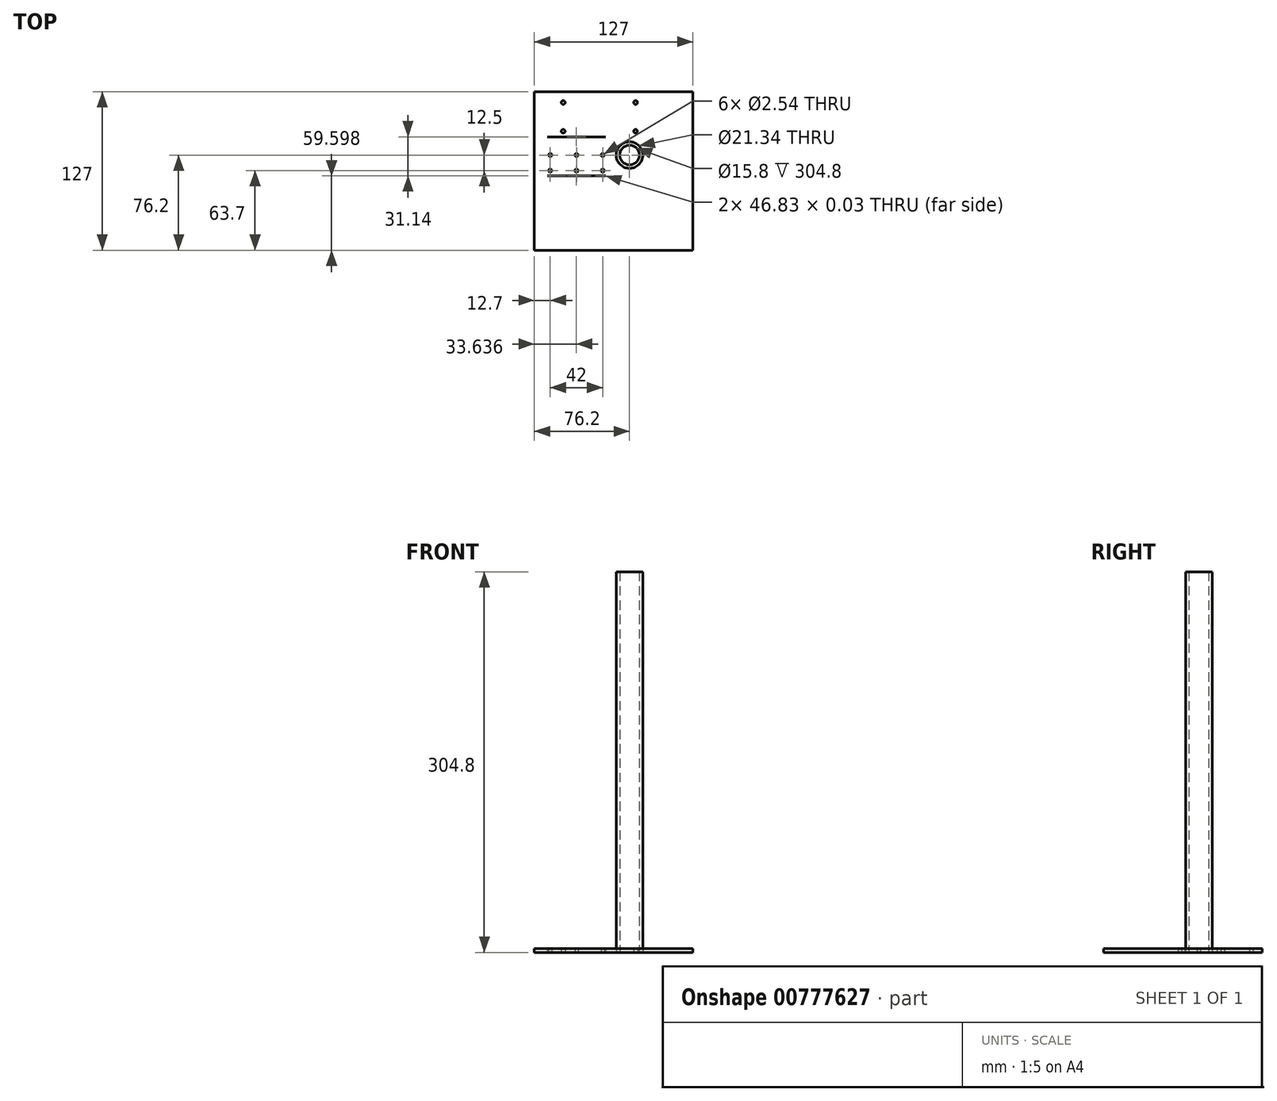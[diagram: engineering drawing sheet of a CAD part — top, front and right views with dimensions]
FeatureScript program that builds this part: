
annotation { "Feature Type Name" : "Feature", "Feature Type Description" : "" }
export const myFeature = defineFeature(function(context is Context, id is Id, definition is map)
    precondition{}
    {
        {
            var Q0;
            Q0=qCreatedBy(makeId("Top.planeOp"),FACE);
            var sketch = newSketch(context, id + "F0", { "sketchPlane" : qUnion([Q0])});
            skCircle(sketch, "E0", {"center": v(0, 0) * mm, "radius": 10.67 * mm});
            skCircle(sketch, "E1", {"center": v(0, 0) * mm, "radius": 7.9 * mm});
            skSolve(sketch);
        }
        {
            var Q0;
            Q0=makeQuery(id+"F0.imprint","IMPRINT",FACE,{"disambiguationData":[TD([[makeQuery(id+"F0.imprint","IMPRINT",EDGE,{"derivedFrom":sQuery(id+"F0.wireOp",EDGE,"E0")}),1.0]])]});
            extrude(context, id + "F1", {"entities" : qUnion([Q0]), "depth" : 304.8 * mm, "offsetDistance" : 25.4 * mm});
        }
        {
            var Q0;
            Q0=makeQuery(id+"F1.opExtrude","CAP_FACE",FACE,{"disambiguationData":[OSD([sQuery(id+"F0.wireOp",EDGE,"E0"),sQuery(id+"F0.wireOp",EDGE,"E1")])],"isStart":true});
            var sketch = newSketch(context, id + "F2", { "sketchPlane" : qUnion([Q0])});
            skLineSegment(sketch, "E2.bottom", {"start": v(50.8, 76.2) * mm, "end": v(-76.2, 76.2) * mm});
            skLineSegment(sketch, "E2.top", {"start": v(50.8, -50.8) * mm, "end": v(-76.2, -50.8) * mm});
            skLineSegment(sketch, "E2.right", {"start": v(-76.2, 76.2) * mm, "end": v(-76.2, -50.8) * mm});
            skLineSegment(sketch, "E3", {"start": v(50.8, 76.2) * mm, "end": v(50.8, -50.8) * mm});
            skSolve(sketch);
        }
        {
            var Q0;
            Q0=makeQuery(id+"F2.imprint","IMPRINT",FACE,{"disambiguationData":[TD([[makeQuery(id+"F2.imprint","IMPRINT",EDGE,{"derivedFrom":sQuery(id+"F2.wireOp",EDGE,"E2.bottom")}),1.0]])]});
            extrude(context, id + "F3", {"entities" : qUnion([Q0]), "oppositeDirection" : true, "depth" : 3.17 * mm, "offsetDistance" : 25.4 * mm});
        }
        {
            var Q0;
            Q0=makeQuery(id+"F3.opExtrude","CAP_FACE",FACE,{"disambiguationData":[OSD([sQuery(id+"F0.wireOp",EDGE,"E0"),sQuery(id+"F2.wireOp",EDGE,"bcf234af-44ee-4ac4-8bec-e13de90e0a41.0"),sQuery(id+"F2.wireOp",EDGE,"E2.bottom"),sQuery(id+"F2.wireOp",EDGE,"E2.top"),sQuery(id+"F2.wireOp",EDGE,"E2.right")])],"isStart":true});
            var sketch = newSketch(context, id + "F4", { "sketchPlane" : qUnion([Q0])});
            skLineSegment(sketch, "E4", {"start": v(-83.28, 24.72) * mm, "end": v(-33.72, 24.72) * mm, "construction": true});
            skCircle(sketch, "E5", {"center": v(-63.5, 0) * mm, "radius": 1.27 * mm});
            skCircle(sketch, "E6.0.1.0", {"center": v(-63.5, 12.5) * mm, "radius": 1.27 * mm});
            skCircle(sketch, "E6.1.0.0", {"center": v(-42.5, 0) * mm, "radius": 1.27 * mm});
            skCircle(sketch, "E6.1.1.0", {"center": v(-42.5, 12.5) * mm, "radius": 1.27 * mm});
            skCircle(sketch, "E6.2.0.0", {"center": v(-21.5, 0) * mm, "radius": 1.27 * mm});
            skCircle(sketch, "E6.2.1.0", {"center": v(-21.5, 12.5) * mm, "radius": 1.27 * mm});
            skLineSegment(sketch, "E6.direction1", {"start": v(-63.5, 0) * mm, "end": v(-42.5, 0) * mm, "construction": true});
            skLineSegment(sketch, "E6.direction2", {"start": v(-63.5, 12.5) * mm, "end": v(-63.5, 0) * mm, "construction": true});
            skLineSegment(sketch, "E7.bottom", {"start": v(-65.98, 16.62) * mm, "end": v(-19.15, 16.62) * mm});
            skLineSegment(sketch, "E7.top", {"start": v(-65.98, 16.59) * mm, "end": v(-19.15, 16.59) * mm});
            skLineSegment(sketch, "E7.left", {"start": v(-65.98, 16.62) * mm, "end": v(-65.98, 16.59) * mm});
            skLineSegment(sketch, "E7.right", {"start": v(-19.15, 16.62) * mm, "end": v(-19.15, 16.59) * mm});
            skLineSegment(sketch, "E8.0.1.0", {"start": v(-65.98, -14.53) * mm, "end": v(-19.15, -14.53) * mm});
            skLineSegment(sketch, "E8.0.1.1", {"start": v(-19.15, -14.53) * mm, "end": v(-19.15, -14.55) * mm});
            skLineSegment(sketch, "E8.0.1.2", {"start": v(-65.98, -14.55) * mm, "end": v(-19.15, -14.55) * mm});
            skLineSegment(sketch, "E8.0.1.3", {"start": v(-65.98, -14.53) * mm, "end": v(-65.98, -14.55) * mm});
            skLineSegment(sketch, "E8.direction1", {"start": v(-65.98, 16.62) * mm, "end": v(-40.58, 16.62) * mm, "construction": true});
            skLineSegment(sketch, "E8.direction2", {"start": v(-65.98, 16.62) * mm, "end": v(-65.98, -14.53) * mm, "construction": true});
            skSolve(sketch);
        }
        {
            var Q0;
            Q0=qSketchRegion(id+"F4",true);
            extrude(context, id + "F5", {"entities" : qUnion([Q0]), "operationType" : NewBodyOperationType.REMOVE, "endBound" : BoundingType.UP_TO_NEXT, "oppositeDirection" : true, "depth" : 25.4 * mm, "offsetDistance" : 25.4 * mm});
        }
        {
            var Q0;
            Q0=makeQuery(id+"F3.opExtrude","CAP_FACE",FACE,{"disambiguationData":[OSD([sQuery(id+"F0.wireOp",EDGE,"E0"),sQuery(id+"F2.wireOp",EDGE,"bcf234af-44ee-4ac4-8bec-e13de90e0a41.0"),sQuery(id+"F2.wireOp",EDGE,"E2.bottom"),sQuery(id+"F2.wireOp",EDGE,"E2.top"),sQuery(id+"F2.wireOp",EDGE,"E2.right")])],"isStart":true});
            var sketch = newSketch(context, id + "F6", { "sketchPlane" : qUnion([Q0])});
            skCircle(sketch, "E9", {"center": v(-53.11, -19.05) * mm, "radius": 1.5 * mm});
            skCircle(sketch, "E10.0.1.0", {"center": v(-53.11, -42.05) * mm, "radius": 1.5 * mm});
            skCircle(sketch, "E10.1.0.0", {"center": v(4.89, -19.05) * mm, "radius": 1.5 * mm});
            skCircle(sketch, "E10.1.1.0", {"center": v(4.89, -42.05) * mm, "radius": 1.5 * mm});
            skLineSegment(sketch, "E10.direction1", {"start": v(-53.11, -19.05) * mm, "end": v(4.9, -19.05) * mm, "construction": true});
            skLineSegment(sketch, "E10.direction2", {"start": v(-53.1, -19.05) * mm, "end": v(-53.1, -42.05) * mm, "construction": true});
            skSolve(sketch);
        }
        {
            var Q0;
            Q0=qSketchRegion(id+"F6",true);
            extrude(context, id + "F7", {"entities" : qUnion([Q0]), "operationType" : NewBodyOperationType.REMOVE, "endBound" : BoundingType.UP_TO_NEXT, "oppositeDirection" : true, "depth" : 25.4 * mm, "offsetDistance" : 25.4 * mm});
        }
    });
